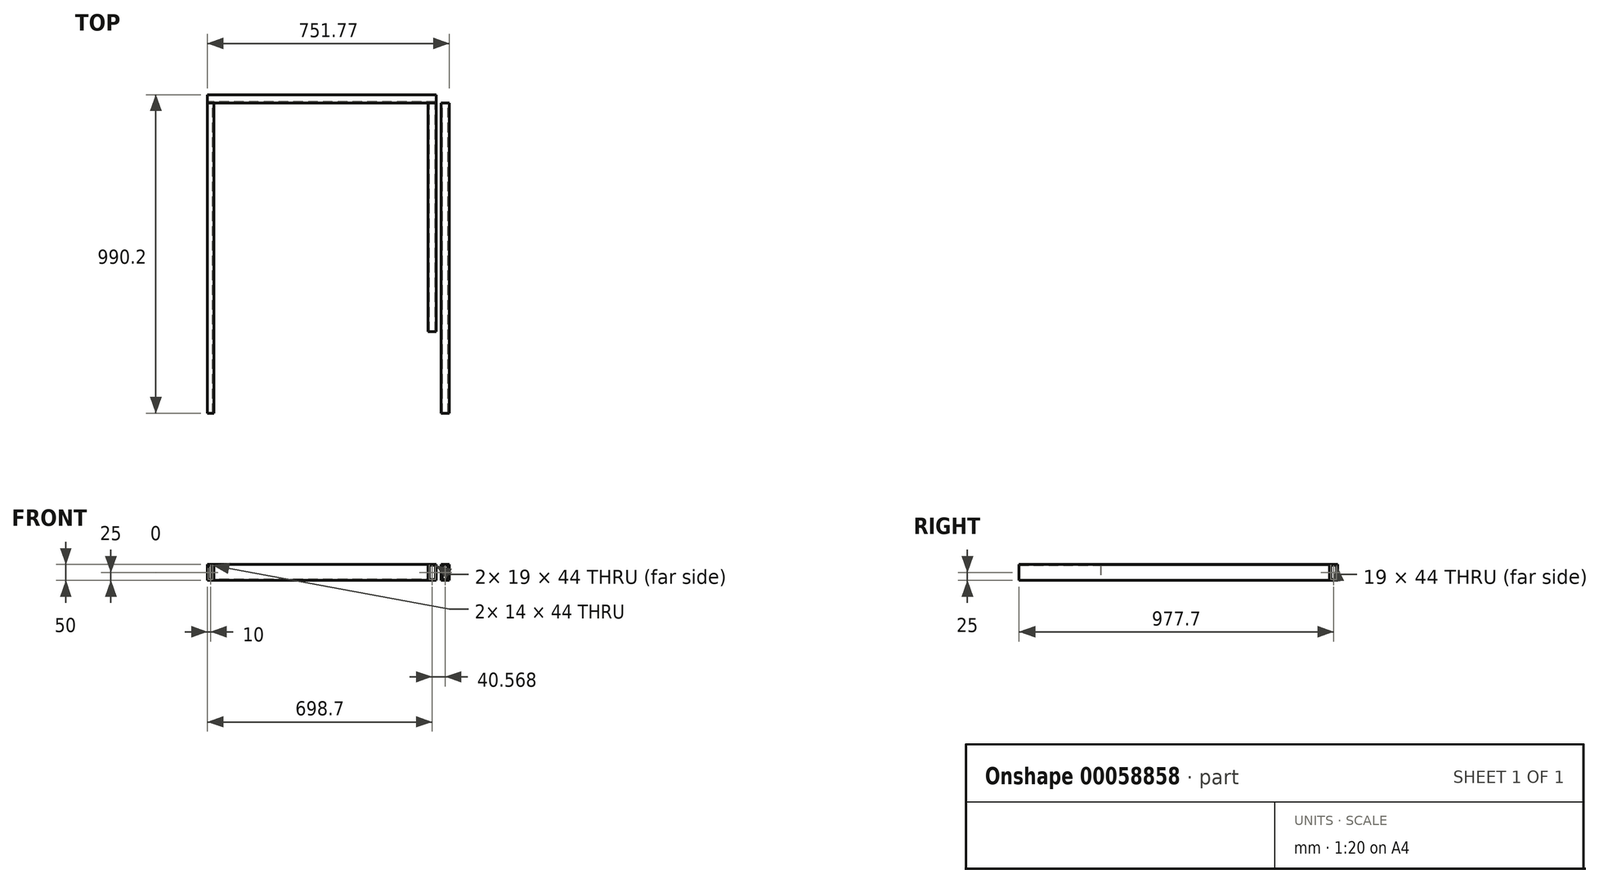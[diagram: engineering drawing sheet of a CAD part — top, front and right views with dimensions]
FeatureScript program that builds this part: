
annotation { "Feature Type Name" : "Feature", "Feature Type Description" : "" }
export const myFeature = defineFeature(function(context is Context, id is Id, definition is map)
    precondition{}
    {
        {
            var Q0;
            Q0=qCreatedBy(makeId("Front.planeOp"),FACE);
            var sketch = newSketch(context, id + "F0", { "sketchPlane" : qUnion([Q0])});
            skLineSegment(sketch, "E0.bottom", {"start": v(0, 0) * mm, "end": v(-20, 0) * mm});
            skLineSegment(sketch, "E0.top", {"start": v(0, 50) * mm, "end": v(-20, 50) * mm});
            skLineSegment(sketch, "E0.left", {"start": v(0, 0) * mm, "end": v(0, 50) * mm});
            skLineSegment(sketch, "E0.right", {"start": v(-20, 0) * mm, "end": v(-20, 50) * mm});
            skLineSegment(sketch, "E1.bottom", {"start": v(-3, 3) * mm, "end": v(-17, 3) * mm});
            skLineSegment(sketch, "E1.top", {"start": v(-3, 47) * mm, "end": v(-17, 47) * mm});
            skLineSegment(sketch, "E1.left", {"start": v(-3, 3) * mm, "end": v(-3, 47) * mm});
            skLineSegment(sketch, "E1.right", {"start": v(-17, 3) * mm, "end": v(-17, 47) * mm});
            skSolve(sketch);
        }
        {
            var Q0;
            Q0=makeQuery(id+"F0.imprint","IMPRINT",FACE,{"disambiguationData":[TD([[makeQuery(id+"F0.imprint","IMPRINT",EDGE,{"derivedFrom":sQuery(id+"F0.wireOp",EDGE,"E0.bottom")}),-1.0]])]});
            extrude(context, id + "F1", {"entities" : qUnion([Q0]), "depth" : 965.2 * mm});
        }
        {
            var Q0;
            Q0=makeQuery(id+"F1.opExtrude","SWEPT_BODY",BODY,{"disambiguationData":[OSD([sQuery(id+"F0.wireOp",EDGE,"E0.bottom"),sQuery(id+"F0.wireOp",EDGE,"E0.top"),sQuery(id+"F0.wireOp",EDGE,"E0.left"),sQuery(id+"F0.wireOp",EDGE,"E0.right"),sQuery(id+"F0.wireOp",EDGE,"E1.bottom"),sQuery(id+"F0.wireOp",EDGE,"E1.top"),sQuery(id+"F0.wireOp",EDGE,"E1.left"),sQuery(id+"F0.wireOp",EDGE,"E1.right")])]});
            transform(context, id + "F2", {"entities" : qUnion([Q0]), "transformType" : TransformType.TRANSLATION_3D, "dx" : 0 * mm, "dy" : 0 * mm, "dz" : 0 * mm, "makeCopy" : true});
        }
        {
            var Q0;
            Q0=qCreatedBy(makeId("Front.planeOp"),FACE);
            var sketch = newSketch(context, id + "F3", { "sketchPlane" : qUnion([Q0])});
            skLineSegment(sketch, "E2.bottom", {"start": v(706.77, 0) * mm, "end": v(731.77, 0) * mm});
            skLineSegment(sketch, "E2.top", {"start": v(706.77, 50) * mm, "end": v(731.77, 50) * mm});
            skLineSegment(sketch, "E2.left", {"start": v(706.77, 0) * mm, "end": v(706.77, 50) * mm});
            skLineSegment(sketch, "E2.right", {"start": v(731.77, 0) * mm, "end": v(731.77, 50) * mm});
            skLineSegment(sketch, "E3.bottom", {"start": v(709.77, 47) * mm, "end": v(728.77, 47) * mm});
            skLineSegment(sketch, "E3.top", {"start": v(709.77, 3) * mm, "end": v(728.77, 3) * mm});
            skLineSegment(sketch, "E3.left", {"start": v(709.77, 47) * mm, "end": v(709.77, 3) * mm});
            skLineSegment(sketch, "E3.right", {"start": v(728.77, 47) * mm, "end": v(728.77, 3) * mm});
            skSolve(sketch);
        }
        {
            var Q0;
            Q0=qSketchRegion(id+"F3",true);
            extrude(context, id + "F4", {"entities" : qUnion([Q0]), "operationType" : NewBodyOperationType.ADD, "depth" : 965.2 * mm});
        }
        {
            var Q0;
            Q0=makeQuery(id+"F1.opExtrude","SWEPT_FACE",FACE,{"disambiguationData":[OSD([sQuery(id+"F0.wireOp",EDGE,"E0.right")])]});
            var sketch = newSketch(context, id + "F5", { "sketchPlane" : qUnion([Q0])});
            skLineSegment(sketch, "E4.bottom", {"start": v(0, 0) * mm, "end": v(-25, 0) * mm});
            skLineSegment(sketch, "E4.top", {"start": v(0, 50) * mm, "end": v(-25, 50) * mm});
            skLineSegment(sketch, "E4.left", {"start": v(0, 0) * mm, "end": v(0, 50) * mm});
            skLineSegment(sketch, "E4.right", {"start": v(-25, 0) * mm, "end": v(-25, 50) * mm});
            skLineSegment(sketch, "E5.bottom", {"start": v(0, 50) * mm, "end": v(0, 50) * mm});
            skLineSegment(sketch, "E5.top", {"start": v(0, 50) * mm, "end": v(0, 50) * mm});
            skLineSegment(sketch, "E5.left", {"start": v(0, 50) * mm, "end": v(0, 50) * mm});
            skLineSegment(sketch, "E5.right", {"start": v(0, 50) * mm, "end": v(0, 50) * mm});
            skLineSegment(sketch, "E6.0", {"start": v(-3, 3) * mm, "end": v(-22, 3) * mm});
            skLineSegment(sketch, "E6.1", {"start": v(-3, 3) * mm, "end": v(-3, 47) * mm});
            skLineSegment(sketch, "E6.2", {"start": v(-3, 47) * mm, "end": v(-22, 47) * mm});
            skLineSegment(sketch, "E6.3", {"start": v(-22, 3) * mm, "end": v(-22, 47) * mm});
            skSolve(sketch);
        }
        {
            var Q0;
            Q0=makeQuery(id+"F5.imprint","IMPRINT",FACE,{"disambiguationData":[TD([[makeQuery(id+"F5.imprint","IMPRINT",EDGE,{"derivedFrom":sQuery(id+"F5.wireOp",EDGE,"E4.bottom")}),-1.0]])]});
            extrude(context, id + "F6", {"entities" : qUnion([Q0]), "oppositeDirection" : true, "depth" : 711.2 * mm});
        }
        {
            var Q0;
            Q0=makeQuery(id+"F6.opExtrude","SWEPT_FACE",FACE,{"disambiguationData":[OSD([sQuery(id+"F5.wireOp",EDGE,"E4.left")])]});
            var sketch = newSketch(context, id + "F7", { "sketchPlane" : qUnion([Q0])});
            skLineSegment(sketch, "E7.bottom", {"start": v(691.2, 50) * mm, "end": v(666.2, 50) * mm});
            skLineSegment(sketch, "E7.top", {"start": v(691.2, 0) * mm, "end": v(666.2, 0) * mm});
            skLineSegment(sketch, "E7.left", {"start": v(691.2, 50) * mm, "end": v(691.2, 0) * mm});
            skLineSegment(sketch, "E7.right", {"start": v(666.2, 50) * mm, "end": v(666.2, 0) * mm});
            skLineSegment(sketch, "E8.bottom", {"start": v(669.2, 47) * mm, "end": v(688.2, 47) * mm});
            skLineSegment(sketch, "E8.top", {"start": v(669.2, 3) * mm, "end": v(688.2, 3) * mm});
            skLineSegment(sketch, "E8.left", {"start": v(669.2, 47) * mm, "end": v(669.2, 3) * mm});
            skLineSegment(sketch, "E8.right", {"start": v(688.2, 47) * mm, "end": v(688.2, 3) * mm});
            skSolve(sketch);
        }
        {
            var Q0;
            Q0=qSketchRegion(id+"F7",true);
            extrude(context, id + "F8", {"entities" : qUnion([Q0]), "depth" : 711.2 * mm});
        }
    });
